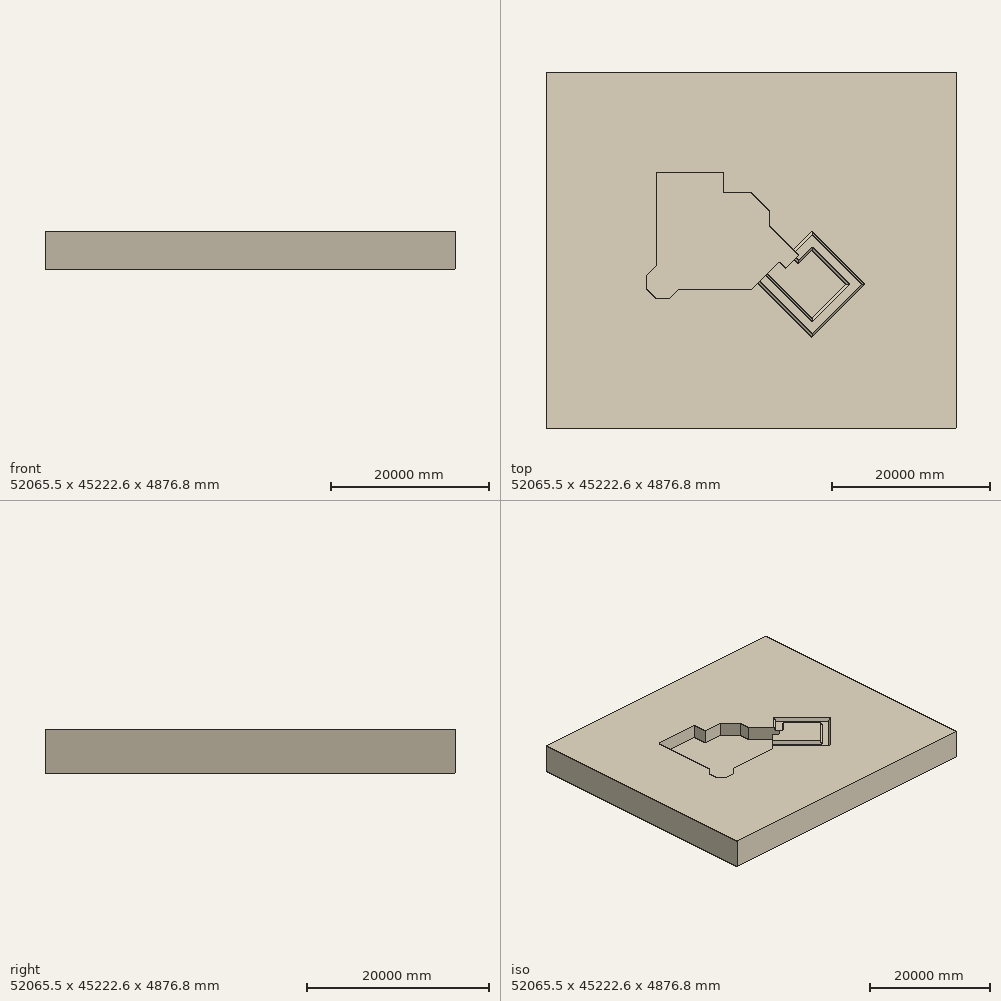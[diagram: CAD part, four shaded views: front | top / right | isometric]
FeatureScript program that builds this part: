
annotation { "Feature Type Name" : "Feature", "Feature Type Description" : "" }
export const myFeature = defineFeature(function(context is Context, id is Id, definition is map)
    precondition{}
    {
        {
            var Q0;
            Q0=qCreatedBy(makeId("Top.planeOp"),FACE);
            var sketch = newSketch(context, id + "F0", { "sketchPlane" : qUnion([Q0])});
            skLineSegment(sketch, "E0", {"start": v(0, 0) * mm, "end": v(-9299.78, 0) * mm});
            skLineSegment(sketch, "E1", {"start": v(-9423.4, 298.45) * mm, "end": v(-123.62, 298.45) * mm});
            skLineSegment(sketch, "E2", {"start": v(0, 0) * mm, "end": v(1293.16, 1293.16) * mm});
            skLineSegment(sketch, "E3", {"start": v(-123.62, 298.45) * mm, "end": v(3410.25, 3832.32) * mm});
            skLineSegment(sketch, "E4", {"start": v(-647.7, 0) * mm, "end": v(-647.7, 298.45) * mm, "construction": true});
            skLineSegment(sketch, "E5", {"start": v(170.62, 170.62) * mm, "end": v(-40.41, 381.66) * mm, "construction": true});
            skLineSegment(sketch, "E6", {"start": v(-1866.9, 0) * mm, "end": v(-1866.9, 298.45) * mm, "construction": true});
            skLineSegment(sketch, "E7", {"start": v(-3086.1, 0) * mm, "end": v(-3086.1, 298.45) * mm, "construction": true});
            skLineSegment(sketch, "E8", {"start": v(-4305.3, 0) * mm, "end": v(-4305.3, 298.45) * mm, "construction": true});
            skLineSegment(sketch, "E9", {"start": v(-5524.5, 0) * mm, "end": v(-5524.5, 298.45) * mm, "construction": true});
            skLineSegment(sketch, "E10", {"start": v(-6743.7, 0) * mm, "end": v(-6743.7, 298.45) * mm, "construction": true});
            skLineSegment(sketch, "E11", {"start": v(-7962.9, 0) * mm, "end": v(-7962.9, 298.45) * mm, "construction": true});
            skLineSegment(sketch, "E12", {"start": v(-9182.1, 0) * mm, "end": v(-9182.1, 298.45) * mm, "construction": true});
            skLineSegment(sketch, "E13", {"start": v(1032.73, 1032.73) * mm, "end": v(821.7, 1243.77) * mm, "construction": true});
            skLineSegment(sketch, "E14", {"start": v(1894.83, 1894.83) * mm, "end": v(1683.8, 2105.87) * mm, "construction": true});
            skLineSegment(sketch, "E15", {"start": v(-9423.4, 298.45) * mm, "end": v(-10683.02, -961.17) * mm});
            skLineSegment(sketch, "E16", {"start": v(-9299.78, 0) * mm, "end": v(-10559.4, -1259.62) * mm});
            skLineSegment(sketch, "E17", {"start": v(-9881.4, -159.54) * mm, "end": v(-9670.36, -370.58) * mm, "construction": true});
            skLineSegment(sketch, "E18", {"start": v(-10559.4, -1259.62) * mm, "end": v(-12261.2, -1259.62) * mm});
            skLineSegment(sketch, "E19", {"start": v(-10683.02, -961.17) * mm, "end": v(-12137.58, -961.17) * mm});
            skLineSegment(sketch, "E20", {"start": v(-10388.78, -1089) * mm, "end": v(-10599.81, -877.96) * mm, "construction": true});
            skLineSegment(sketch, "E21", {"start": v(-11207.1, -1259.62) * mm, "end": v(-11207.1, -961.17) * mm, "construction": true});
            skLineSegment(sketch, "E22", {"start": v(-12137.58, -961.17) * mm, "end": v(-13166.1, 67.35) * mm});
            skLineSegment(sketch, "E23", {"start": v(-13166.1, 67.35) * mm, "end": v(-13166.1, 1521.9) * mm});
            skLineSegment(sketch, "E24", {"start": v(-13166.1, 1521.9) * mm, "end": v(-11906.48, 2781.53) * mm});
            skLineSegment(sketch, "E25", {"start": v(-11906.48, 2781.53) * mm, "end": v(-11906.48, 14513.16) * mm});
            skLineSegment(sketch, "E26", {"start": v(-12261.2, -1259.62) * mm, "end": v(-13464.56, -56.27) * mm});
            skLineSegment(sketch, "E27", {"start": v(-13464.56, -56.27) * mm, "end": v(-13464.56, 1645.53) * mm});
            skLineSegment(sketch, "E28", {"start": v(-13464.56, 1645.53) * mm, "end": v(-12204.93, 2905.15) * mm});
            skLineSegment(sketch, "E29", {"start": v(-12204.93, 2905.15) * mm, "end": v(-12204.93, 14811.6) * mm});
            skLineSegment(sketch, "E30", {"start": v(-12019.9, -1259.62) * mm, "end": v(-12019.9, -961.17) * mm, "construction": true});
            skLineSegment(sketch, "E31", {"start": v(-12719.2, -801.63) * mm, "end": v(-12508.16, -590.6) * mm, "construction": true});
            skLineSegment(sketch, "E32", {"start": v(-13293.93, -226.9) * mm, "end": v(-13082.9, -15.86) * mm, "construction": true});
            skLineSegment(sketch, "E33", {"start": v(-13464.56, 591.43) * mm, "end": v(-13166.1, 591.43) * mm, "construction": true});
            skLineSegment(sketch, "E34", {"start": v(-13464.56, 1404.23) * mm, "end": v(-13166.1, 1404.23) * mm, "construction": true});
            skLineSegment(sketch, "E35", {"start": v(-13006.56, 2103.52) * mm, "end": v(-12795.53, 1892.49) * mm, "construction": true});
            skLineSegment(sketch, "E36", {"start": v(-12288.14, 2821.94) * mm, "end": v(-12077.1, 2610.9) * mm, "construction": true});
            skLineSegment(sketch, "E37", {"start": v(-12204.93, 3429.23) * mm, "end": v(-11906.48, 3429.23) * mm, "construction": true});
            skLineSegment(sketch, "E38", {"start": v(-12204.93, 14811.6) * mm, "end": v(-3664.18, 14811.6) * mm});
            skLineSegment(sketch, "E39", {"start": v(-11906.48, 14513.16) * mm, "end": v(-3962.63, 14513.16) * mm});
            skLineSegment(sketch, "E40", {"start": v(-12204.93, 4648.43) * mm, "end": v(-11906.48, 4648.43) * mm, "construction": true});
            skLineSegment(sketch, "E41", {"start": v(-12204.93, 5867.63) * mm, "end": v(-11906.48, 5867.63) * mm, "construction": true});
            skLineSegment(sketch, "E42", {"start": v(-12204.93, 7086.83) * mm, "end": v(-11906.48, 7086.83) * mm, "construction": true});
            skLineSegment(sketch, "E43", {"start": v(-12204.93, 8306.03) * mm, "end": v(-11906.48, 8306.03) * mm, "construction": true});
            skLineSegment(sketch, "E44", {"start": v(-12204.93, 9525.23) * mm, "end": v(-11906.48, 9525.23) * mm, "construction": true});
            skLineSegment(sketch, "E45", {"start": v(-12204.93, 10744.43) * mm, "end": v(-11906.48, 10744.43) * mm, "construction": true});
            skLineSegment(sketch, "E46", {"start": v(-12204.93, 11963.63) * mm, "end": v(-11906.48, 11963.63) * mm, "construction": true});
            skLineSegment(sketch, "E47", {"start": v(-12204.93, 13182.83) * mm, "end": v(-11906.48, 13182.83) * mm, "construction": true});
            skLineSegment(sketch, "E48", {"start": v(-11388.96, 14811.6) * mm, "end": v(-11388.96, 14513.16) * mm, "construction": true});
            skLineSegment(sketch, "E49", {"start": v(-3962.63, 14513.16) * mm, "end": v(-3962.63, 11960.46) * mm});
            skLineSegment(sketch, "E50", {"start": v(-3962.63, 11960.46) * mm, "end": v(-286.18, 11960.46) * mm});
            skLineSegment(sketch, "E51", {"start": v(-3664.18, 14811.6) * mm, "end": v(-3664.18, 12258.9) * mm});
            skLineSegment(sketch, "E52", {"start": v(-3664.18, 12258.9) * mm, "end": v(-162.56, 12258.9) * mm});
            skLineSegment(sketch, "E53", {"start": v(-4073.76, 14513.16) * mm, "end": v(-4073.76, 14811.6) * mm, "construction": true});
            skLineSegment(sketch, "E54", {"start": v(-3962.63, 12776.43) * mm, "end": v(-3664.18, 12776.43) * mm, "construction": true});
            skLineSegment(sketch, "E55", {"start": v(-10169.76, 14513.16) * mm, "end": v(-10169.76, 14811.6) * mm, "construction": true});
            skLineSegment(sketch, "E56", {"start": v(-8950.56, 14513.16) * mm, "end": v(-8950.56, 14811.6) * mm, "construction": true});
            skLineSegment(sketch, "E57", {"start": v(-7731.36, 14513.16) * mm, "end": v(-7731.36, 14811.6) * mm, "construction": true});
            skLineSegment(sketch, "E58", {"start": v(-6512.16, 14513.16) * mm, "end": v(-6512.16, 14811.6) * mm, "construction": true});
            skLineSegment(sketch, "E59", {"start": v(1293.16, 1293.16) * mm, "end": v(7597.3, -5010.98) * mm});
            skLineSegment(sketch, "E60", {"start": v(7597.3, -4813.42) * mm, "end": v(1391.94, 1391.94) * mm});
            skLineSegment(sketch, "E61", {"start": v(1391.94, 1391.94) * mm, "end": v(3410.25, 3410.25) * mm});
            skLineSegment(sketch, "E62", {"start": v(3410.25, 3410.25) * mm, "end": v(4209.5, 2611) * mm});
            skLineSegment(sketch, "E63", {"start": v(4209.5, 2611) * mm, "end": v(5867.83, 4269.34) * mm});
            skLineSegment(sketch, "E64", {"start": v(5445.76, 4269.34) * mm, "end": v(4209.5, 3033.08) * mm});
            skLineSegment(sketch, "E65", {"start": v(4209.5, 3033.08) * mm, "end": v(3410.25, 3832.32) * mm});
            skLineSegment(sketch, "E66", {"start": v(2833.27, 3255.34) * mm, "end": v(3044.3, 3044.3) * mm, "construction": true});
            skLineSegment(sketch, "E67", {"start": v(2545.9, 2967.97) * mm, "end": v(2756.94, 2756.94) * mm, "construction": true});
            skLineSegment(sketch, "E68", {"start": v(3488.83, 3331.68) * mm, "end": v(3699.87, 3542.71) * mm, "construction": true});
            skLineSegment(sketch, "E69", {"start": v(3632.51, 3188) * mm, "end": v(3843.55, 3399.03) * mm, "construction": true});
            skLineSegment(sketch, "E70", {"start": v(4288.07, 3111.66) * mm, "end": v(4499.1, 2900.62) * mm, "construction": true});
            skLineSegment(sketch, "E71", {"start": v(5769.05, 4368.13) * mm, "end": v(2190.27, 7946.9) * mm});
            skLineSegment(sketch, "E72", {"start": v(5445.76, 4269.34) * mm, "end": v(1891.82, 7823.28) * mm});
            skLineSegment(sketch, "E73", {"start": v(5079.81, 3903.4) * mm, "end": v(5290.85, 3692.36) * mm, "construction": true});
            skLineSegment(sketch, "E74", {"start": v(5367.18, 4347.92) * mm, "end": v(5578.22, 4558.96) * mm, "construction": true});
            skLineSegment(sketch, "E75", {"start": v(2190.27, 7946.9) * mm, "end": v(2190.27, 9906.08) * mm});
            skLineSegment(sketch, "E76", {"start": v(2190.27, 9906.08) * mm, "end": v(-162.56, 12258.9) * mm});
            skLineSegment(sketch, "E77", {"start": v(1891.82, 7823.28) * mm, "end": v(1891.82, 9782.46) * mm});
            skLineSegment(sketch, "E78", {"start": v(1891.82, 9782.46) * mm, "end": v(-286.18, 11960.46) * mm});
            skLineSegment(sketch, "E79", {"start": v(2349.81, 7365.29) * mm, "end": v(2560.85, 7576.32) * mm, "construction": true});
            skLineSegment(sketch, "E80", {"start": v(1891.82, 8064.58) * mm, "end": v(2190.27, 8064.58) * mm, "construction": true});
            skLineSegment(sketch, "E81", {"start": v(3211.92, 6503.18) * mm, "end": v(3422.95, 6714.22) * mm, "construction": true});
            skLineSegment(sketch, "E82", {"start": v(4074.02, 5641.08) * mm, "end": v(4285.06, 5852.11) * mm, "construction": true});
            skLineSegment(sketch, "E83", {"start": v(4936.13, 4778.97) * mm, "end": v(5147.16, 4990) * mm, "construction": true});
            skLineSegment(sketch, "E84", {"start": v(1891.82, 9258.38) * mm, "end": v(2190.27, 9258.38) * mm, "construction": true});
            skLineSegment(sketch, "E85", {"start": v(1808.61, 9865.67) * mm, "end": v(2019.65, 10076.7) * mm, "construction": true});
            skLineSegment(sketch, "E86", {"start": v(84.4, 11589.88) * mm, "end": v(295.44, 11800.91) * mm, "construction": true});
            skLineSegment(sketch, "E87", {"start": v(-403.86, 11960.46) * mm, "end": v(-403.86, 12258.9) * mm, "construction": true});
            skLineSegment(sketch, "E88", {"start": v(-3146.66, 11960.46) * mm, "end": v(-3146.66, 12258.9) * mm, "construction": true});
            skLineSegment(sketch, "E89", {"start": v(-3962.63, 12370.03) * mm, "end": v(-3664.18, 12370.03) * mm, "construction": true});
            skLineSegment(sketch, "E90", {"start": v(946.5, 10727.77) * mm, "end": v(1157.54, 10938.8) * mm, "construction": true});
            skLineSegment(sketch, "E91", {"start": v(-1927.46, 12258.9) * mm, "end": v(-1927.46, 11960.46) * mm, "construction": true});
            skLineSegment(sketch, "E92", {"start": v(-708.26, 12258.9) * mm, "end": v(-708.26, 11960.46) * mm, "construction": true});
            skLineSegment(sketch, "E93", {"start": v(7597.3, -4813.42) * mm, "end": v(13003.41, 592.7) * mm});
            skLineSegment(sketch, "E94", {"start": v(13003.41, 592.7) * mm, "end": v(7597.3, 5998.81) * mm});
            skLineSegment(sketch, "E95", {"start": v(7597.3, 5998.81) * mm, "end": v(5867.83, 4269.34) * mm});
            skLineSegment(sketch, "E96", {"start": v(7597.3, -5010.98) * mm, "end": v(13200.98, 592.7) * mm});
            skLineSegment(sketch, "E97", {"start": v(13200.98, 592.7) * mm, "end": v(7597.3, 6196.38) * mm});
            skLineSegment(sketch, "E98", {"start": v(7597.3, 6196.38) * mm, "end": v(5769.05, 4368.13) * mm});
            skLineSegment(sketch, "E99.0", {"start": v(4209.5, 2709.8) * mm, "end": v(5769.05, 4269.34) * mm});
            skLineSegment(sketch, "E99.1", {"start": v(3410.25, 3509.04) * mm, "end": v(4209.5, 2709.8) * mm});
            skLineSegment(sketch, "E99.2", {"start": v(-28.93, 69.85) * mm, "end": v(1243.77, 1342.55) * mm});
            skLineSegment(sketch, "E100.0", {"start": v(5670.26, 4368.13) * mm, "end": v(2120.42, 7917.97) * mm});
            skLineSegment(sketch, "E100.1", {"start": v(2120.42, 7917.97) * mm, "end": v(2120.42, 9877.15) * mm});
            skLineSegment(sketch, "E100.2", {"start": v(2120.42, 9877.15) * mm, "end": v(-191.49, 12189.06) * mm});
            skLineSegment(sketch, "E100.3", {"start": v(-3734.03, 12189.06) * mm, "end": v(-191.49, 12189.06) * mm});
            skLineSegment(sketch, "E100.4", {"start": v(-3734.03, 14741.76) * mm, "end": v(-3734.03, 12189.06) * mm});
            skLineSegment(sketch, "E100.5", {"start": v(-12232.27, -1189.77) * mm, "end": v(-13394.7, -27.34) * mm});
            skLineSegment(sketch, "E100.6", {"start": v(-10588.34, -1189.77) * mm, "end": v(-12232.27, -1189.77) * mm});
            skLineSegment(sketch, "E100.7", {"start": v(-9328.71, 69.85) * mm, "end": v(-10588.34, -1189.77) * mm});
            skLineSegment(sketch, "E100.8", {"start": v(-28.93, 69.85) * mm, "end": v(-9328.71, 69.85) * mm});
            skLineSegment(sketch, "E100.9", {"start": v(-13394.7, -27.34) * mm, "end": v(-13394.7, 1616.6) * mm});
            skLineSegment(sketch, "E100.10", {"start": v(-13394.7, 1616.6) * mm, "end": v(-12135.08, 2876.22) * mm});
            skLineSegment(sketch, "E100.11", {"start": v(-12135.08, 2876.22) * mm, "end": v(-12135.08, 14741.76) * mm});
            skLineSegment(sketch, "E100.13", {"start": v(-12135.08, 14741.76) * mm, "end": v(-3734.03, 14741.76) * mm});
            skLineSegment(sketch, "E101.0", {"start": v(5544.54, 4269.34) * mm, "end": v(4209.5, 2934.3) * mm});
            skLineSegment(sketch, "E101.1", {"start": v(4209.5, 2934.3) * mm, "end": v(3410.25, 3733.54) * mm});
            skLineSegment(sketch, "E101.2", {"start": v(-94.69, 228.6) * mm, "end": v(3410.25, 3733.54) * mm});
            skLineSegment(sketch, "E101.3", {"start": v(-9394.47, 228.6) * mm, "end": v(-94.69, 228.6) * mm});
            skLineSegment(sketch, "E101.4", {"start": v(-9394.47, 228.6) * mm, "end": v(-10654.1, -1031.02) * mm});
            skLineSegment(sketch, "E101.5", {"start": v(5544.54, 4269.34) * mm, "end": v(1961.67, 7852.21) * mm});
            skLineSegment(sketch, "E101.6", {"start": v(-10654.1, -1031.02) * mm, "end": v(-12166.51, -1031.02) * mm});
            skLineSegment(sketch, "E101.7", {"start": v(-12166.51, -1031.02) * mm, "end": v(-13235.96, 38.42) * mm});
            skLineSegment(sketch, "E101.8", {"start": v(-3892.78, 14583) * mm, "end": v(-3892.78, 12030.3) * mm});
            skLineSegment(sketch, "E101.9", {"start": v(-3892.78, 12030.3) * mm, "end": v(-257.25, 12030.3) * mm});
            skLineSegment(sketch, "E101.10", {"start": v(1961.67, 9811.4) * mm, "end": v(-257.25, 12030.3) * mm});
            skLineSegment(sketch, "E101.11", {"start": v(1961.67, 7852.21) * mm, "end": v(1961.67, 9811.4) * mm});
            skLineSegment(sketch, "E101.13", {"start": v(-11976.33, 14583) * mm, "end": v(-3892.78, 14583) * mm});
            skLineSegment(sketch, "E101.15", {"start": v(-11976.33, 2810.47) * mm, "end": v(-11976.33, 14583) * mm});
            skLineSegment(sketch, "E101.16", {"start": v(-13235.96, 1550.84) * mm, "end": v(-11976.33, 2810.47) * mm});
            skLineSegment(sketch, "E101.17", {"start": v(-13235.96, 38.42) * mm, "end": v(-13235.96, 1550.84) * mm});
            skLineSegment(sketch, "E102", {"start": v(5769.05, 4368.13) * mm, "end": v(5670.26, 4368.13) * mm});
            skLineSegment(sketch, "E103", {"start": v(5867.83, 4269.34) * mm, "end": v(5769.05, 4269.34) * mm});
            skLineSegment(sketch, "E104", {"start": v(1391.94, 1391.94) * mm, "end": v(1342.55, 1441.33) * mm});
            skLineSegment(sketch, "E105", {"start": v(1293.16, 1293.16) * mm, "end": v(1243.77, 1342.55) * mm});
            skLineSegment(sketch, "E106.trimOffspring", {"start": v(1342.55, 1441.33) * mm, "end": v(3410.25, 3509.04) * mm});
            skLineSegment(sketch, "E107", {"start": v(-12204.93, 14402.03) * mm, "end": v(-11906.48, 14402.03) * mm, "construction": true});
            skLineSegment(sketch, "E108", {"start": v(-5292.96, 14811.6) * mm, "end": v(-5292.96, 14513.16) * mm, "construction": true});
            skLineSegment(sketch, "E109", {"start": v(-3962.63, 13995.63) * mm, "end": v(-3664.18, 13995.63) * mm, "construction": true});
            skSolve(sketch);
        }
        {
            var Q0;
            Q0=qCreatedBy(makeId("Top.planeOp"),FACE);
            var sketch = newSketch(context, id + "F1", { "sketchPlane" : qUnion([Q0])});
            skLineSegment(sketch, "E110.bottom", {"start": v(-26164.56, 27511.6) * mm, "end": v(25900.98, 27511.6) * mm});
            skLineSegment(sketch, "E110.top", {"start": v(-26164.56, -17710.98) * mm, "end": v(25900.98, -17710.98) * mm});
            skLineSegment(sketch, "E110.left", {"start": v(-26164.56, 27511.6) * mm, "end": v(-26164.56, -17710.98) * mm});
            skLineSegment(sketch, "E110.right", {"start": v(25900.98, 27511.6) * mm, "end": v(25900.98, -17710.98) * mm});
            skSolve(sketch);
        }
        {
            var Q0;
            Q0 = qSketchRegion(id + "F1", true);
            extrude(context, id + "F2", {"entities" : qUnion([Q0]), "oppositeDirection" : true, "depth" : 5080 * mm, "offsetDistance" : 25.4 * mm});
        }
        {
            var Q0;
            Q0=makeQuery(id+"F2.opExtrude","CAP_FACE",FACE,{"disambiguationData":[OSD([sQuery(id+"F1.wireOp",EDGE,"E110.bottom"),sQuery(id+"F1.wireOp",EDGE,"E110.top"),sQuery(id+"F1.wireOp",EDGE,"E110.left"),sQuery(id+"F1.wireOp",EDGE,"E110.right")])],"isStart":true});
            var sketch = newSketch(context, id + "F3", { "sketchPlane" : qUnion([Q0])});
            skLineSegment(sketch, "E111", {"start": v(-12204.93, 14811.6) * mm, "end": v(-3664.18, 14811.6) * mm});
            skLineSegment(sketch, "E112", {"start": v(-3664.18, 14811.6) * mm, "end": v(-3664.18, 12258.9) * mm});
            skLineSegment(sketch, "E113", {"start": v(-3664.18, 12258.9) * mm, "end": v(-162.56, 12258.9) * mm});
            skLineSegment(sketch, "E114", {"start": v(-162.56, 12258.9) * mm, "end": v(2190.27, 9906.08) * mm});
            skLineSegment(sketch, "E115", {"start": v(2190.27, 9906.08) * mm, "end": v(2190.27, 7946.9) * mm});
            skLineSegment(sketch, "E116", {"start": v(2190.27, 7946.9) * mm, "end": v(5867.83, 4269.34) * mm});
            skLineSegment(sketch, "E117", {"start": v(5867.83, 4269.34) * mm, "end": v(4209.5, 2611) * mm});
            skLineSegment(sketch, "E118", {"start": v(4209.5, 2611) * mm, "end": v(3410.25, 3410.25) * mm});
            skLineSegment(sketch, "E119", {"start": v(3410.25, 3410.25) * mm, "end": v(0, 0) * mm});
            skLineSegment(sketch, "E120", {"start": v(0, 0) * mm, "end": v(-9299.78, 0) * mm});
            skLineSegment(sketch, "E121", {"start": v(-9299.78, 0) * mm, "end": v(-10559.4, -1259.62) * mm});
            skLineSegment(sketch, "E122", {"start": v(-10559.4, -1259.62) * mm, "end": v(-12261.2, -1259.62) * mm});
            skLineSegment(sketch, "E123", {"start": v(-12261.2, -1259.62) * mm, "end": v(-13464.56, -56.27) * mm});
            skLineSegment(sketch, "E124", {"start": v(-13464.56, -56.27) * mm, "end": v(-13464.56, 1645.53) * mm});
            skLineSegment(sketch, "E125", {"start": v(-13464.56, 1645.53) * mm, "end": v(-12204.93, 2905.15) * mm});
            skLineSegment(sketch, "E126", {"start": v(-12204.93, 2905.15) * mm, "end": v(-12204.93, 14811.6) * mm});
            skSolve(sketch);
        }
        {
            var Q0;
            Q0 = qSketchRegion(id + "F3", true);
            extrude(context, id + "F4", {"entities" : qUnion([Q0]), "operationType" : NewBodyOperationType.REMOVE, "oppositeDirection" : true, "depth" : 2540 * mm, "offsetDistance" : 25.4 * mm});
        }
        {
            var Q0;
            Q0=makeQuery(id+"F2.opExtrude","CAP_FACE",FACE,{"disambiguationData":[OSD([sQuery(id+"F1.wireOp",EDGE,"E110.bottom"),sQuery(id+"F1.wireOp",EDGE,"E110.top"),sQuery(id+"F1.wireOp",EDGE,"E110.left"),sQuery(id+"F1.wireOp",EDGE,"E110.right")])],"isStart":true});
            var sketch = newSketch(context, id + "F5", { "sketchPlane" : qUnion([Q0])});
            skLineSegment(sketch, "E127", {"start": v(1293.16, 1293.16) * mm, "end": v(1391.94, 1391.94) * mm});
            skLineSegment(sketch, "E128", {"start": v(1391.94, 1391.94) * mm, "end": v(7597.3, -4813.42) * mm});
            skLineSegment(sketch, "E129", {"start": v(7597.3, -4813.42) * mm, "end": v(13003.41, 592.7) * mm});
            skLineSegment(sketch, "E130", {"start": v(13003.41, 592.7) * mm, "end": v(7597.3, 5998.81) * mm});
            skLineSegment(sketch, "E131", {"start": v(7597.3, 5998.81) * mm, "end": v(5867.83, 4269.34) * mm});
            skLineSegment(sketch, "E132", {"start": v(5867.83, 4269.34) * mm, "end": v(5769.05, 4368.13) * mm});
            skLineSegment(sketch, "E133", {"start": v(5769.05, 4368.13) * mm, "end": v(7597.3, 6196.38) * mm});
            skLineSegment(sketch, "E134", {"start": v(7597.3, 6196.38) * mm, "end": v(13200.98, 592.7) * mm});
            skLineSegment(sketch, "E135", {"start": v(13200.98, 592.7) * mm, "end": v(7597.3, -5010.98) * mm});
            skLineSegment(sketch, "E136", {"start": v(7597.3, -5010.98) * mm, "end": v(1293.16, 1293.16) * mm});
            skSolve(sketch);
        }
        {
            var Q0;
            Q0 = qSketchRegion(id + "F5", true);
            extrude(context, id + "F6", {"entities" : qUnion([Q0]), "operationType" : NewBodyOperationType.REMOVE, "oppositeDirection" : true, "depth" : 762 * mm, "offsetDistance" : 25.4 * mm});
        }
        {
            var Q0;
            Q0=makeQuery(id+"F0.imprint","IMPRINT",FACE,{"disambiguationData":[TD([[makeQuery(id+"F0.imprint","IMPRINT",EDGE,{"derivedFrom":sQuery(id+"F0.wireOp",EDGE,"E60")}),-1.0]])]});
            extrude(context, id + "F7", {"entities" : qUnion([Q0]), "operationType" : NewBodyOperationType.REMOVE, "oppositeDirection" : true, "depth" : 228.6 * mm, "offsetDistance" : 25.4 * mm});
        }
        {
            var Q0;
            {var subQ0=sQuery(id+"F1.wireOp",EDGE,"E110.bottom");var subQ1=sQuery(id+"F1.wireOp",EDGE,"E110.right");var subQ2=sQuery(id+"F1.wireOp",EDGE,"E110.top");var subQ3=sQuery(id+"F1.wireOp",EDGE,"E110.left");Q0=makeQuery(id+"F6.boolean.opBoolean","SPLIT",FACE,{"disambiguationData":[TD([makeQuery(id+"F2.opExtrude","SWEPT_FACE",FACE,{"disambiguationData":[OSD([subQ0])]})])],"derivedFrom":makeQuery(id+"F2.opExtrude","CAP_FACE",FACE,{"disambiguationData":[OSD([subQ0,subQ2,subQ3,subQ1])],"isStart":true})});}
            var sketch = newSketch(context, id + "F8", { "sketchPlane" : qUnion([Q0])});
            skLineSegment(sketch, "E137", {"start": v(1284.18, 1284.18) * mm, "end": v(7597.3, -5028.94) * mm});
            skLineSegment(sketch, "E138", {"start": v(7597.3, -5028.94) * mm, "end": v(13218.94, 592.7) * mm});
            skLineSegment(sketch, "E139", {"start": v(13218.94, 592.7) * mm, "end": v(7597.3, 6214.34) * mm});
            skLineSegment(sketch, "E140", {"start": v(7597.3, 6214.34) * mm, "end": v(5760.07, 4377.1) * mm});
            skLineSegment(sketch, "E141", {"start": v(5760.07, 4377.1) * mm, "end": v(5769.05, 4368.13) * mm});
            skLineSegment(sketch, "E142", {"start": v(5769.05, 4368.13) * mm, "end": v(7597.3, 6196.38) * mm});
            skLineSegment(sketch, "E143", {"start": v(7597.3, 6196.38) * mm, "end": v(13200.98, 592.7) * mm});
            skLineSegment(sketch, "E144", {"start": v(13200.98, 592.7) * mm, "end": v(7597.3, -5010.98) * mm});
            skLineSegment(sketch, "E145", {"start": v(7597.3, -5010.98) * mm, "end": v(1293.16, 1293.16) * mm});
            skLineSegment(sketch, "E146", {"start": v(1293.16, 1293.16) * mm, "end": v(1284.18, 1284.18) * mm});
            skSolve(sketch);
        }
        {
            var Q0;
            Q0 = qSketchRegion(id + "F8", true);
            var Q1;
            Q1=makeQuery(id+"F6.boolean.opBoolean","COPY",FACE,{"derivedFrom":makeQuery(id+"F6.opExtrude","CAP_FACE",FACE,{"disambiguationData":[OSD([sQuery(id+"F5.wireOp",EDGE,"E127"),sQuery(id+"F5.wireOp",EDGE,"E128"),sQuery(id+"F5.wireOp",EDGE,"E129"),sQuery(id+"F5.wireOp",EDGE,"E130"),sQuery(id+"F5.wireOp",EDGE,"E131"),sQuery(id+"F5.wireOp",EDGE,"E132"),sQuery(id+"F5.wireOp",EDGE,"E133"),sQuery(id+"F5.wireOp",EDGE,"E134"),sQuery(id+"F5.wireOp",EDGE,"E135"),sQuery(id+"F5.wireOp",EDGE,"E136")])],"isStart":false})});
            extrude(context, id + "F9", {"entities" : qUnion([Q0]), "operationType" : NewBodyOperationType.REMOVE, "endBound" : BoundingType.UP_TO_SURFACE, "oppositeDirection" : true, "depth" : 25.4 * mm, "endBoundEntityFace" : qUnion([Q1]), "offsetDistance" : 25.4 * mm});
        }
        {
            var Q0;
            {var subQ0=sQuery(id+"F1.wireOp",EDGE,"E110.bottom");var subQ1=sQuery(id+"F1.wireOp",EDGE,"E110.right");var subQ2=sQuery(id+"F1.wireOp",EDGE,"E110.top");var subQ3=sQuery(id+"F1.wireOp",EDGE,"E110.left");Q0=makeQuery(id+"F6.boolean.opBoolean","SPLIT",FACE,{"disambiguationData":[TD([makeQuery(id+"F2.opExtrude","SWEPT_FACE",FACE,{"disambiguationData":[OSD([subQ0])]})])],"derivedFrom":makeQuery(id+"F2.opExtrude","CAP_FACE",FACE,{"disambiguationData":[OSD([subQ0,subQ2,subQ3,subQ1])],"isStart":true})});}
            extrude(context, id + "F10", {"entities" : qUnion([Q0]), "operationType" : NewBodyOperationType.REMOVE, "oppositeDirection" : true, "depth" : 203.2 * mm, "offsetDistance" : 25.4 * mm});
        }
        {
            var Q0;
            Q0=makeQuery(id+"F4.boolean.opBoolean","COPY",FACE,{"derivedFrom":makeQuery(id+"F4.opExtrude","SWEPT_FACE",FACE,{"disambiguationData":[OSD([sQuery(id+"F3.wireOp",EDGE,"E119")])]})});
            var sketch = newSketch(context, id + "F11", { "sketchPlane" : qUnion([Q0])});
            skLineSegment(sketch, "E147", {"start": v(-2733.66, -228.6) * mm, "end": v(-2425.7, -762) * mm});
            skLineSegment(sketch, "E148", {"start": v(-2425.7, -762) * mm, "end": v(-1358.9, -762) * mm});
            skLineSegment(sketch, "E149", {"start": v(-1358.9, -762) * mm, "end": v(-1036.28, -203.2) * mm});
            skLineSegment(sketch, "E150", {"start": v(-1036.28, -203.2) * mm, "end": v(-2733.66, -203.2) * mm});
            skLineSegment(sketch, "E151", {"start": v(-2733.66, -203.2) * mm, "end": v(-2733.66, -228.6) * mm});
            skSolve(sketch);
        }
        {
            var Q0;
            Q0 = qSketchRegion(id + "F11", true);
            var Q1;
            Q1=makeQuery(id+"F6.boolean.opBoolean","COPY",EDGE,{"derivedFrom":makeQuery(id+"F6.opExtrude","CAP_EDGE",EDGE,{"disambiguationData":[OSD([sQuery(id+"F5.wireOp",EDGE,"E128")])],"isStart":false})});
            var Q2;
            Q2=makeQuery(id+"F6.boolean.opBoolean","COPY",EDGE,{"derivedFrom":makeQuery(id+"F6.opExtrude","CAP_EDGE",EDGE,{"disambiguationData":[OSD([sQuery(id+"F5.wireOp",EDGE,"E129")])],"isStart":false})});
            var Q3;
            Q3=makeQuery(id+"F6.boolean.opBoolean","COPY",EDGE,{"derivedFrom":makeQuery(id+"F6.opExtrude","CAP_EDGE",EDGE,{"disambiguationData":[OSD([sQuery(id+"F5.wireOp",EDGE,"E130")])],"isStart":false})});
            var Q4;
            Q4=makeQuery(id+"F6.boolean.opBoolean","COPY",EDGE,{"derivedFrom":makeQuery(id+"F6.opExtrude","CAP_EDGE",EDGE,{"disambiguationData":[OSD([sQuery(id+"F5.wireOp",EDGE,"E131")])],"isStart":false})});
            sweep(context, id + "F12", {"operationType" : NewBodyOperationType.REMOVE, "profiles" : qUnion([Q0]), "path" : qUnion([Q1, Q2, Q3, Q4])});
        }
        {
            var Q0;
            Q0=makeQuery(id+"F6.boolean.opBoolean","MERGE",FACE,{"derivedFrom":[makeQuery(id+"F4.boolean.opBoolean","COPY",FACE,{"derivedFrom":makeQuery(id+"F4.opExtrude","SWEPT_FACE",FACE,{"disambiguationData":[OSD([sQuery(id+"F3.wireOp",EDGE,"E117")])]})})],"fromTools":[makeQuery(id+"F6.opExtrude","SWEPT_FACE",FACE,{"disambiguationData":[OSD([sQuery(id+"F5.wireOp",EDGE,"E131")])]})]});
            var sketch = newSketch(context, id + "F13", { "sketchPlane" : qUnion([Q0])});
            skLineSegment(sketch, "E152", {"start": v(-7168.06, -762) * mm, "end": v(-6710.86, -762) * mm});
            skLineSegment(sketch, "E153", {"start": v(-6710.86, -762) * mm, "end": v(-6402.9, -228.6) * mm});
            skLineSegment(sketch, "E154", {"start": v(-6402.9, -228.6) * mm, "end": v(-7168.06, -228.6) * mm});
            skLineSegment(sketch, "E155", {"start": v(-7168.06, -228.6) * mm, "end": v(-7168.06, -762) * mm});
            skSolve(sketch);
        }
        {
            var Q0;
            Q0 = qSketchRegion(id + "F13", true);
            var Q1;
            Q1=makeQuery(id+"F12.boolean.opBoolean","COPY",FACE,{"derivedFrom":makeQuery(id+"F12.opSweep","SWEPT_FACE",FACE,{"disambiguationData":[OSD([sQuery(id+"F5.wireOp",EDGE,"E131"),sQuery(id+"F11.wireOp",EDGE,"E147")])]})});
            extrude(context, id + "F14", {"entities" : qUnion([Q0]), "operationType" : NewBodyOperationType.REMOVE, "endBound" : BoundingType.UP_TO_SURFACE, "oppositeDirection" : true, "depth" : 25.4 * mm, "endBoundEntityFace" : qUnion([Q1]), "offsetDistance" : 25.4 * mm});
        }
    });
